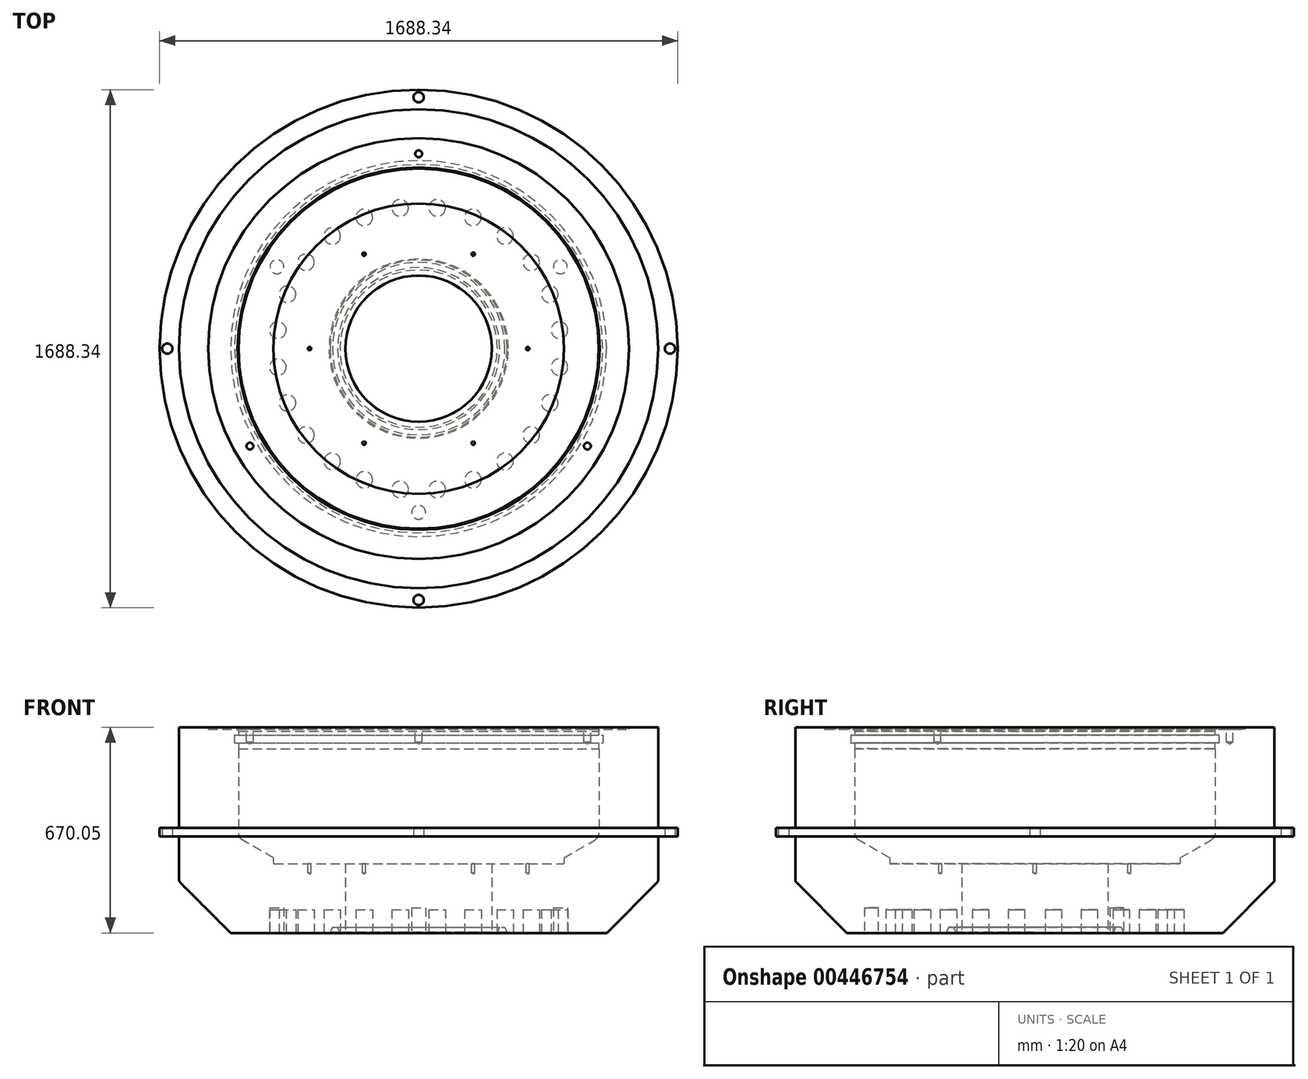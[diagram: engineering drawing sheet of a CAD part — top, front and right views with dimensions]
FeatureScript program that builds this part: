
annotation { "Feature Type Name" : "Feature", "Feature Type Description" : "" }
export const myFeature = defineFeature(function(context is Context, id is Id, definition is map)
    precondition{}
    {
        {
            var Q0;
            Q0=qCreatedBy(makeId("Right.planeOp"),FACE);
            var sketch = newSketch(context, id + "F0", { "sketchPlane" : qUnion([Q0])});
            skLineSegment(sketch, "E0", {"start": v(685.8, 0) * mm, "end": v(780.67, 0) * mm});
            skLineSegment(sketch, "E1", {"start": v(780.67, 0) * mm, "end": v(780.67, -327.03) * mm});
            skLineSegment(sketch, "E2", {"start": v(780.67, -327.03) * mm, "end": v(844.17, -327.03) * mm});
            skLineSegment(sketch, "E3", {"start": v(844.17, -327.03) * mm, "end": v(844.17, -355.6) * mm});
            skLineSegment(sketch, "E4", {"start": v(844.17, -355.6) * mm, "end": v(780.67, -355.6) * mm});
            skLineSegment(sketch, "E5", {"start": v(780.67, -355.6) * mm, "end": v(780.67, -502.16) * mm});
            skLineSegment(sketch, "E6", {"start": v(780.67, -502.16) * mm, "end": v(612.77, -670.05) * mm});
            skLineSegment(sketch, "E7", {"start": v(612.78, -670.05) * mm, "end": v(288.98, -670.05) * mm});
            skLineSegment(sketch, "E8", {"start": v(0, -670.05) * mm, "end": v(0, 0) * mm, "construction": true});
            skLineSegment(sketch, "E9", {"start": v(288.98, -670.05) * mm, "end": v(281.1, -651.5) * mm});
            skLineSegment(sketch, "E10", {"start": v(281.1, -651.5) * mm, "end": v(264.03, -651.5) * mm});
            skLineSegment(sketch, "E11", {"start": v(264.03, -651.5) * mm, "end": v(256.16, -670.05) * mm});
            skLineSegment(sketch, "E12.trimOffspring", {"start": v(256.16, -670.05) * mm, "end": v(238.32, -670.05) * mm});
            skLineSegment(sketch, "E13", {"start": v(238.32, -670.05) * mm, "end": v(238.32, -444.5) * mm});
            skLineSegment(sketch, "E14", {"start": v(238.32, -444.5) * mm, "end": v(473.14, -444.5) * mm});
            skLineSegment(sketch, "E15", {"start": v(473.14, -444.5) * mm, "end": v(473.14, -425.45) * mm});
            skLineSegment(sketch, "E16", {"start": v(473.14, -425.45) * mm, "end": v(574.68, -366.83) * mm});
            skLineSegment(sketch, "E17", {"start": v(587.38, -344.83) * mm, "end": v(587.38, -69.9) * mm});
            skLineSegment(sketch, "E18", {"start": v(587.38, -69.9) * mm, "end": v(586.61, -69.9) * mm});
            skLineSegment(sketch, "E19", {"start": v(586.61, -69.9) * mm, "end": v(586.61, -50.85) * mm});
            skLineSegment(sketch, "E20", {"start": v(586.61, -50.85) * mm, "end": v(600.08, -50.85) * mm});
            skLineSegment(sketch, "E21", {"start": v(600.08, -50.85) * mm, "end": v(600.08, -25.45) * mm});
            skLineSegment(sketch, "E22", {"start": v(600.08, -25.45) * mm, "end": v(586.61, -25.45) * mm});
            skLineSegment(sketch, "E23", {"start": v(586.61, -25.45) * mm, "end": v(586.61, -12.75) * mm});
            skLineSegment(sketch, "E24", {"start": v(586.61, -12.75) * mm, "end": v(590.28, -6.4) * mm});
            skLineSegment(sketch, "E25", {"start": v(590.28, -6.4) * mm, "end": v(685.8, -6.4) * mm});
            skLineSegment(sketch, "E26", {"start": v(685.8, -6.4) * mm, "end": v(685.8, 0) * mm});
            skPoint(sketch, "E27.visualSharp", {"position": v(587.38, -359.5) * mm});
            skArc(sketch, "E27.filletArc", {"start": v(574.68, -366.83) * mm, "mid": v(583.97, -357.53) * mm, "end": v(587.38, -344.83) * mm});
            skSolve(sketch);
        }
        {
            var Q0;
            Q0=makeQuery(id+"F0.imprint","IMPRINT",FACE,{"disambiguationData":[TD([[makeQuery(id+"F0.imprint","IMPRINT",EDGE,{"derivedFrom":sQuery(id+"F0.wireOp",EDGE,"E0")}),-1.0]])]});
            var Q1;
            Q1=sQuery(id+"F0.wireOp",EDGE,"E8");
            revolve(context, id + "F1", {"entities" : qUnion([Q0]), "axis" : qUnion([Q1]), "revolveType" : RevolveType.FULL});
        }
        {
            var Q0;
            Q0=makeQuery(id+"F1.opRevolve","SWEPT_FACE",FACE,{"disambiguationData":[OSD([sQuery(id+"F0.wireOp",EDGE,"E7")])]});
            var sketch = newSketch(context, id + "F2", { "sketchPlane" : qUnion([Q0])});
            skCircle(sketch, "E28", {"center": v(0, 0) * mm, "radius": 238.32 * mm});
            skSolve(sketch);
        }
        {
            var Q0;
            Q0=makeQuery(id+"F2.imprint","IMPRINT",FACE,{"disambiguationData":[TD([[makeQuery(id+"F2.imprint","IMPRINT",EDGE,{"derivedFrom":sQuery(id+"F2.wireOp",EDGE,"E28")}),1.0]])]});
            extrude(context, id + "F3", {"entities" : qUnion([Q0]), "operationType" : NewBodyOperationType.REMOVE, "endBound" : BoundingType.THROUGH_ALL, "oppositeDirection" : true, "depth" : 25.4 * mm});
        }
        {
            var Q0;
            Q0=makeQuery(id+"F2.imprint","IMPRINT",FACE,{"disambiguationData":[TD([[makeQuery(id+"F2.imprint","IMPRINT",EDGE,{"derivedFrom":sQuery(id+"F2.wireOp",EDGE,"E28")}),-1.0]])]});
            var sketch = newSketch(context, id + "F4", { "sketchPlane" : qUnion([Q0])});
            skCircle(sketch, "E29", {"center": v(0, 0) * mm, "radius": 533.4 * mm, "construction": true});
            skLineSegment(sketch, "E30", {"start": v(0, 576.2) * mm, "end": v(0, -586.92) * mm, "construction": true});
            skLineSegment(sketch, "E31", {"start": v(-569.53, 0) * mm, "end": v(569.53, 0) * mm, "construction": true});
            skCircle(sketch, "E32", {"center": v(0, 533.4) * mm, "radius": 22.62 * mm});
            skCircle(sketch, "E33.1.0", {"center": v(-461.94, -266.7) * mm, "radius": 22.62 * mm});
            skCircle(sketch, "E33.2.0", {"center": v(461.94, -266.7) * mm, "radius": 22.62 * mm});
            skPoint(sketch, "E34", {"position": v(-533.4, 0) * mm});
            skCircle(sketch, "E35", {"center": v(0, 0) * mm, "radius": 462.76 * mm, "construction": true});
            skCircle(sketch, "E36", {"center": v(0, 462.76) * mm, "radius": 27.01 * mm});
            skCircle(sketch, "E37.1.0", {"center": v(-119.77, 447) * mm, "radius": 27.01 * mm});
            skCircle(sketch, "E37.2.0", {"center": v(-231.38, 400.76) * mm, "radius": 27.01 * mm});
            skCircle(sketch, "E37.3.0", {"center": v(-327.22, 327.22) * mm, "radius": 27.01 * mm});
            skCircle(sketch, "E37.4.0", {"center": v(-400.76, 231.38) * mm, "radius": 27.01 * mm});
            skCircle(sketch, "E37.5.0", {"center": v(-447, 119.77) * mm, "radius": 27.01 * mm});
            skCircle(sketch, "E37.6.0", {"center": v(-462.76, 0) * mm, "radius": 27.01 * mm});
            skCircle(sketch, "E37.7.0", {"center": v(-447, -119.77) * mm, "radius": 27.01 * mm});
            skCircle(sketch, "E37.8.0", {"center": v(-400.76, -231.38) * mm, "radius": 27.01 * mm});
            skCircle(sketch, "E37.9.0", {"center": v(-327.22, -327.22) * mm, "radius": 27.01 * mm});
            skCircle(sketch, "E37.10.0", {"center": v(-231.38, -400.76) * mm, "radius": 27.01 * mm});
            skCircle(sketch, "E37.11.0", {"center": v(-119.77, -447) * mm, "radius": 27.01 * mm});
            skCircle(sketch, "E37.12.0", {"center": v(0, -462.76) * mm, "radius": 27.01 * mm});
            skCircle(sketch, "E37.13.0", {"center": v(119.77, -447) * mm, "radius": 27.01 * mm});
            skCircle(sketch, "E37.14.0", {"center": v(231.38, -400.76) * mm, "radius": 27.01 * mm});
            skCircle(sketch, "E37.15.0", {"center": v(327.22, -327.22) * mm, "radius": 27.01 * mm});
            skCircle(sketch, "E37.16.0", {"center": v(400.76, -231.38) * mm, "radius": 27.01 * mm});
            skCircle(sketch, "E37.17.0", {"center": v(447, -119.77) * mm, "radius": 27.01 * mm});
            skCircle(sketch, "E37.18.0", {"center": v(462.76, 0) * mm, "radius": 27.01 * mm});
            skCircle(sketch, "E37.19.0", {"center": v(447, 119.77) * mm, "radius": 27.01 * mm});
            skCircle(sketch, "E37.20.0", {"center": v(400.76, 231.38) * mm, "radius": 27.01 * mm});
            skCircle(sketch, "E37.21.0", {"center": v(327.22, 327.22) * mm, "radius": 27.01 * mm});
            skCircle(sketch, "E37.22.0", {"center": v(231.38, 400.76) * mm, "radius": 27.01 * mm});
            skCircle(sketch, "E37.23.0", {"center": v(119.77, 447) * mm, "radius": 27.01 * mm});
            skSolve(sketch);
        }
        {
            var Q0;
            Q0=makeQuery(id+"F4.imprint","IMPRINT",FACE,{"disambiguationData":[TD([[makeQuery(id+"F4.imprint","IMPRINT",EDGE,{"derivedFrom":sQuery(id+"F4.wireOp",EDGE,"E33.2.0")}),1.0]])]});
            var Q1;
            Q1=makeQuery(id+"F4.imprint","IMPRINT",FACE,{"disambiguationData":[TD([[makeQuery(id+"F4.imprint","IMPRINT",EDGE,{"derivedFrom":sQuery(id+"F4.wireOp",EDGE,"E32")}),1.0]])]});
            var Q2;
            Q2=makeQuery(id+"F4.imprint","IMPRINT",FACE,{"disambiguationData":[TD([[makeQuery(id+"F4.imprint","IMPRINT",EDGE,{"derivedFrom":sQuery(id+"F4.wireOp",EDGE,"E33.1.0")}),1.0]])]});
            var Q3;
            Q3=sQuery(id+"F4.wireOp",EDGE,"E32");
            var Q4;
            Q4=sQuery(id+"F4.wireOp",EDGE,"E33.2.0");
            var Q5;
            Q5=sQuery(id+"F4.wireOp",EDGE,"E33.1.0");
            extrude(context, id + "F5", {"entities" : qUnion([Q0, Q1, Q2]), "operationType" : NewBodyOperationType.REMOVE, "surfaceEntities" : qUnion([Q3, Q4, Q5]), "oppositeDirection" : true, "depth" : 82.55 * mm});
        }
        {
            var Q0;
            Q0=makeQuery(id+"F2.imprint","IMPRINT",FACE,{"disambiguationData":[TD([[makeQuery(id+"F2.imprint","IMPRINT",EDGE,{"derivedFrom":sQuery(id+"F2.wireOp",EDGE,"E28")}),-1.0]])]});
            var sketch = newSketch(context, id + "F6", { "sketchPlane" : qUnion([Q0])});
            skCircle(sketch, "E38", {"center": v(0, 0) * mm, "radius": 462.76 * mm, "construction": true});
            skLineSegment(sketch, "E39", {"start": v(0, -533.44) * mm, "end": v(0, 495.99) * mm, "construction": true});
            skLineSegment(sketch, "E40", {"start": v(-532.1, 0) * mm, "end": v(529.42, 0) * mm, "construction": true});
            skLineSegment(sketch, "E41", {"start": v(0, 0) * mm, "end": v(68.74, 522.11) * mm, "construction": true});
            skCircle(sketch, "E42", {"center": v(60.4, 458.8) * mm, "radius": 27.01 * mm});
            skCircle(sketch, "E43.1.0", {"center": v(-60.4, 458.8) * mm, "radius": 27.01 * mm});
            skCircle(sketch, "E43.2.0", {"center": v(-177.1, 427.54) * mm, "radius": 27.01 * mm});
            skCircle(sketch, "E43.3.0", {"center": v(-281.71, 367.13) * mm, "radius": 27.01 * mm});
            skCircle(sketch, "E43.4.0", {"center": v(-367.13, 281.71) * mm, "radius": 27.01 * mm});
            skCircle(sketch, "E43.5.0", {"center": v(-427.54, 177.1) * mm, "radius": 27.01 * mm});
            skCircle(sketch, "E43.6.0", {"center": v(-458.8, 60.4) * mm, "radius": 27.01 * mm});
            skCircle(sketch, "E43.7.0", {"center": v(-458.8, -60.4) * mm, "radius": 27.01 * mm});
            skCircle(sketch, "E43.8.0", {"center": v(-427.54, -177.1) * mm, "radius": 27.01 * mm});
            skCircle(sketch, "E43.9.0", {"center": v(-367.13, -281.71) * mm, "radius": 27.01 * mm});
            skCircle(sketch, "E43.10.0", {"center": v(-281.71, -367.13) * mm, "radius": 27.01 * mm});
            skCircle(sketch, "E43.11.0", {"center": v(-177.1, -427.54) * mm, "radius": 27.01 * mm});
            skCircle(sketch, "E43.12.0", {"center": v(-60.4, -458.8) * mm, "radius": 27.01 * mm});
            skCircle(sketch, "E43.13.0", {"center": v(60.4, -458.8) * mm, "radius": 27.01 * mm});
            skCircle(sketch, "E43.14.0", {"center": v(177.1, -427.54) * mm, "radius": 27.01 * mm});
            skCircle(sketch, "E43.15.0", {"center": v(281.71, -367.13) * mm, "radius": 27.01 * mm});
            skCircle(sketch, "E43.16.0", {"center": v(367.13, -281.71) * mm, "radius": 27.01 * mm});
            skCircle(sketch, "E43.17.0", {"center": v(427.54, -177.1) * mm, "radius": 27.01 * mm});
            skCircle(sketch, "E43.18.0", {"center": v(458.8, -60.4) * mm, "radius": 27.01 * mm});
            skCircle(sketch, "E43.19.0", {"center": v(458.8, 60.4) * mm, "radius": 27.01 * mm});
            skCircle(sketch, "E43.20.0", {"center": v(427.54, 177.1) * mm, "radius": 27.01 * mm});
            skCircle(sketch, "E43.21.0", {"center": v(367.13, 281.71) * mm, "radius": 27.01 * mm});
            skCircle(sketch, "E43.22.0", {"center": v(281.71, 367.13) * mm, "radius": 27.01 * mm});
            skCircle(sketch, "E43.23.0", {"center": v(177.1, 427.54) * mm, "radius": 27.01 * mm});
            skSolve(sketch);
        }
        {
            var Q0;
            Q0 = qSketchRegion(id + "F6", true);
            extrude(context, id + "F7", {"entities" : qUnion([Q0]), "operationType" : NewBodyOperationType.REMOVE, "oppositeDirection" : true, "depth" : 76.2 * mm});
        }
        {
            var Q0;
            Q0=makeQuery(id+"F1.opRevolve","SWEPT_FACE",FACE,{"disambiguationData":[OSD([sQuery(id+"F0.wireOp",EDGE,"E4")])]});
            var sketch = newSketch(context, id + "F8", { "sketchPlane" : qUnion([Q0])});
            skCircle(sketch, "E44", {"center": v(0, 0) * mm, "radius": 819.15 * mm, "construction": true});
            skLineSegment(sketch, "E45", {"start": v(0, 875.67) * mm, "end": v(0, -893.47) * mm, "construction": true});
            skLineSegment(sketch, "E46", {"start": v(-680.1, 0) * mm, "end": v(709.45, 0) * mm, "construction": true});
            skCircle(sketch, "E47", {"center": v(0, 819.15) * mm, "radius": 16.66 * mm});
            skCircle(sketch, "E48.1.0", {"center": v(-819.15, 0) * mm, "radius": 16.66 * mm});
            skCircle(sketch, "E48.2.0", {"center": v(0, -819.15) * mm, "radius": 16.66 * mm});
            skCircle(sketch, "E48.3.0", {"center": v(819.15, 0) * mm, "radius": 16.66 * mm});
            skSolve(sketch);
        }
        {
            var Q0;
            Q0 = qSketchRegion(id + "F8", true);
            extrude(context, id + "F9", {"entities" : qUnion([Q0]), "operationType" : NewBodyOperationType.REMOVE, "endBound" : BoundingType.THROUGH_ALL, "oppositeDirection" : true, "depth" : 25.4 * mm});
        }
        {
            var Q0;
            Q0=makeQuery(id+"F1.opRevolve","SWEPT_FACE",FACE,{"disambiguationData":[OSD([sQuery(id+"F0.wireOp",EDGE,"E25")])]});
            var sketch = newSketch(context, id + "F10", { "sketchPlane" : qUnion([Q0])});
            skLineSegment(sketch, "E49", {"start": v(0, 869.08) * mm, "end": v(0, -865.75) * mm, "construction": true});
            skLineSegment(sketch, "E50", {"start": v(-898.52, 0) * mm, "end": v(879.6, 0) * mm, "construction": true});
            skCircle(sketch, "E51", {"center": v(0, 0) * mm, "radius": 635 * mm, "construction": true});
            skPoint(sketch, "E52", {"position": v(0, 635) * mm});
            skPoint(sketch, "E53.1.0", {"position": v(-549.93, -317.5) * mm});
            skPoint(sketch, "E53.2.0", {"position": v(549.93, -317.5) * mm});
            skSolve(sketch);
        }
        {
            var Q0;
            Q0=sQuery(id+"F10.wireOp",VERTEX,"E52");
            var Q1;
            Q1=sQuery(id+"F10.wireOp",VERTEX,"E53.1.0");
            var Q2;
            Q2=sQuery(id+"F10.wireOp",VERTEX,"E53.2.0");
            var Q3;
            Q3=makeQuery(id+"F1.opRevolve","SWEPT_BODY",BODY,{"disambiguationData":[OSD([sQuery(id+"F0.wireOp",EDGE,"E0"),sQuery(id+"F0.wireOp",EDGE,"E1"),sQuery(id+"F0.wireOp",EDGE,"E2"),sQuery(id+"F0.wireOp",EDGE,"E3"),sQuery(id+"F0.wireOp",EDGE,"E4"),sQuery(id+"F0.wireOp",EDGE,"E5"),sQuery(id+"F0.wireOp",EDGE,"E6"),sQuery(id+"F0.wireOp",EDGE,"E7"),sQuery(id+"F0.wireOp",EDGE,"E9"),sQuery(id+"F0.wireOp",EDGE,"E10"),sQuery(id+"F0.wireOp",EDGE,"E11"),sQuery(id+"F0.wireOp",EDGE,"E12.trimOffspring"),sQuery(id+"F0.wireOp",EDGE,"E13"),sQuery(id+"F0.wireOp",EDGE,"E14"),sQuery(id+"F0.wireOp",EDGE,"E15"),sQuery(id+"F0.wireOp",EDGE,"E16"),sQuery(id+"F0.wireOp",EDGE,"E17"),sQuery(id+"F0.wireOp",EDGE,"E18"),sQuery(id+"F0.wireOp",EDGE,"E19"),sQuery(id+"F0.wireOp",EDGE,"E20"),sQuery(id+"F0.wireOp",EDGE,"E21"),sQuery(id+"F0.wireOp",EDGE,"E22"),sQuery(id+"F0.wireOp",EDGE,"E23"),sQuery(id+"F0.wireOp",EDGE,"E24"),sQuery(id+"F0.wireOp",EDGE,"E25"),sQuery(id+"F0.wireOp",EDGE,"E26"),sQuery(id+"F0.wireOp",EDGE,"E27.filletArc")])]});
            hole(context, id + "F11", {"style" : HoleStyle.SIMPLE, "endStyle" : HoleEndStyle.BLIND, "standardTappedOrClearance" : lookupTablePath({ "standard" : "ANSI", "engagement" : "75%", "pitch" : "8 tpi", "size" : "1", "type" : "Tapped" }), "standardBlindInLast" : lookupTablePath({ "standard" : "ANSI", "engagement" : "75%", "pitch" : "8 tpi", "size" : "1", "type" : "Tapped" }), "holeDiameter" : 22.22 * mm, "showTappedDepth" : true, "holeDepth" : 41.27 * mm, "isTappedThrough" : true, "tappedDepth" : 28.57 * mm, "tapClearance" : 4, "locations" : qUnion([Q0, Q1, Q2]), "scope" : qUnion([Q3]), "majorDiameter" : 25.4 * mm});
        }
        {
            var Q0;
            Q0=makeQuery(id+"F1.opRevolve","SWEPT_FACE",FACE,{"disambiguationData":[OSD([sQuery(id+"F0.wireOp",EDGE,"E14")])]});
            var sketch = newSketch(context, id + "F12", { "sketchPlane" : qUnion([Q0])});
            skLineSegment(sketch, "E54", {"start": v(-858.3, 0) * mm, "end": v(713.12, 0) * mm, "construction": true});
            skLineSegment(sketch, "E55", {"start": v(0, 688.91) * mm, "end": v(0, -536.12) * mm, "construction": true});
            skCircle(sketch, "E56", {"center": v(0, 0) * mm, "radius": 355.6 * mm, "construction": true});
            skLineSegment(sketch, "E57", {"start": v(0, 0) * mm, "end": v(-195.38, -338.41) * mm, "construction": true});
            skPoint(sketch, "E58", {"position": v(-177.8, -307.96) * mm});
            skPoint(sketch, "E59.1.0", {"position": v(177.8, -307.96) * mm});
            skPoint(sketch, "E59.2.0", {"position": v(355.6, 0) * mm});
            skPoint(sketch, "E59.3.0", {"position": v(177.8, 307.96) * mm});
            skPoint(sketch, "E59.4.0", {"position": v(-177.8, 307.96) * mm});
            skPoint(sketch, "E59.5.0", {"position": v(-355.6, 0) * mm});
            skSolve(sketch);
        }
        {
            var Q0;
            Q0=sQuery(id+"F12.wireOp",VERTEX,"E59.4.0");
            var Q1;
            Q1=sQuery(id+"F12.wireOp",VERTEX,"E59.3.0");
            var Q2;
            Q2=sQuery(id+"F12.wireOp",VERTEX,"E59.2.0");
            var Q3;
            Q3=sQuery(id+"F12.wireOp",VERTEX,"E59.1.0");
            var Q4;
            Q4=sQuery(id+"F12.wireOp",VERTEX,"E58");
            var Q5;
            Q5=sQuery(id+"F12.wireOp",VERTEX,"E59.5.0");
            var Q6;
            Q6=makeQuery(id+"F1.opRevolve","SWEPT_BODY",BODY,{"disambiguationData":[OSD([sQuery(id+"F0.wireOp",EDGE,"E0"),sQuery(id+"F0.wireOp",EDGE,"E1"),sQuery(id+"F0.wireOp",EDGE,"E2"),sQuery(id+"F0.wireOp",EDGE,"E3"),sQuery(id+"F0.wireOp",EDGE,"E4"),sQuery(id+"F0.wireOp",EDGE,"E5"),sQuery(id+"F0.wireOp",EDGE,"E6"),sQuery(id+"F0.wireOp",EDGE,"E7"),sQuery(id+"F0.wireOp",EDGE,"E9"),sQuery(id+"F0.wireOp",EDGE,"E10"),sQuery(id+"F0.wireOp",EDGE,"E11"),sQuery(id+"F0.wireOp",EDGE,"E12.trimOffspring"),sQuery(id+"F0.wireOp",EDGE,"E13"),sQuery(id+"F0.wireOp",EDGE,"E14"),sQuery(id+"F0.wireOp",EDGE,"E15"),sQuery(id+"F0.wireOp",EDGE,"E16"),sQuery(id+"F0.wireOp",EDGE,"E17"),sQuery(id+"F0.wireOp",EDGE,"E18"),sQuery(id+"F0.wireOp",EDGE,"E19"),sQuery(id+"F0.wireOp",EDGE,"E20"),sQuery(id+"F0.wireOp",EDGE,"E21"),sQuery(id+"F0.wireOp",EDGE,"E22"),sQuery(id+"F0.wireOp",EDGE,"E23"),sQuery(id+"F0.wireOp",EDGE,"E24"),sQuery(id+"F0.wireOp",EDGE,"E25"),sQuery(id+"F0.wireOp",EDGE,"E26"),sQuery(id+"F0.wireOp",EDGE,"E27.filletArc")])]});
            hole(context, id + "F13", {"style" : HoleStyle.SIMPLE, "endStyle" : HoleEndStyle.BLIND, "standardTappedOrClearance" : lookupTablePath({ "standard" : "ANSI", "engagement" : "75%", "pitch" : "13 tpi", "size" : "1/2", "type" : "Tapped" }), "standardBlindInLast" : lookupTablePath({ "standard" : "ANSI", "engagement" : "75%", "pitch" : "13 tpi", "size" : "1/2", "type" : "Tapped" }), "holeDiameter" : 10.72 * mm, "showTappedDepth" : true, "holeDepth" : 30.18 * mm, "isTappedThrough" : true, "tappedDepth" : 22.36 * mm, "tapClearance" : 4, "locations" : qUnion([Q0, Q1, Q2, Q3, Q4, Q5]), "scope" : qUnion([Q6]), "majorDiameter" : 12.7 * mm});
        }
        {
            var Q0;
            Q0=makeQuery(id+"F1.opRevolve","SWEPT_EDGE",EDGE,{"disambiguationData":[OSD([sQuery(id+"F0.wireOp",EDGE,"E5"),sQuery(id+"F0.wireOp",EDGE,"E6")])]});
            fillet(context, id + "F14", {"entities" : qUnion([Q0]), "radius" : 12.7 * mm, "tangentPropagation" : true, "allowEdgeOverflow" : false});
        }
        {
            var Q0;
            Q0=makeQuery(id+"F1.opRevolve","SWEPT_EDGE",EDGE,{"disambiguationData":[OSD([sQuery(id+"F0.wireOp",EDGE,"E7"),sQuery(id+"F0.wireOp",EDGE,"E9")])]});
            chamfer(context, id + "F15", {"entities" : qUnion([Q0]), "chamferType" : ChamferType.OFFSET_ANGLE, "width" : 1.57 * mm, "oppositeDirection" : false, "angle" : 45 * degree, "tangentPropagation" : true});
        }
        {
            var Q0;
            Q0=makeQuery(id+"F1.opRevolve","SWEPT_EDGE",EDGE,{"disambiguationData":[OSD([sQuery(id+"F0.wireOp",EDGE,"E12.trimOffspring"),sQuery(id+"F0.wireOp",EDGE,"E13")])]});
            chamfer(context, id + "F16", {"entities" : qUnion([Q0]), "chamferType" : ChamferType.OFFSET_ANGLE, "width" : 1.57 * mm, "oppositeDirection" : false, "angle" : 45 * degree, "tangentPropagation" : true});
        }
        {
            var Q0;
            Q0=makeQuery(id+"F1.opRevolve","SWEPT_EDGE",EDGE,{"disambiguationData":[OSD([sQuery(id+"F0.wireOp",EDGE,"E14"),sQuery(id+"F0.wireOp",EDGE,"E15")])]});
            fillet(context, id + "F17", {"entities" : qUnion([Q0]), "radius" : 2.3 * mm, "tangentPropagation" : true, "allowEdgeOverflow" : false});
        }
        {
            var Q0;
            Q0=makeQuery(id+"F1.opRevolve","SWEPT_EDGE",EDGE,{"disambiguationData":[OSD([sQuery(id+"F0.wireOp",EDGE,"E15"),sQuery(id+"F0.wireOp",EDGE,"E16")])]});
            fillet(context, id + "F18", {"entities" : qUnion([Q0]), "radius" : 0.76 * mm, "tangentPropagation" : true, "allowEdgeOverflow" : false});
        }
        {
            var Q0;
            Q0=makeQuery(id+"F1.opRevolve","SWEPT_EDGE",EDGE,{"disambiguationData":[OSD([sQuery(id+"F0.wireOp",EDGE,"E4"),sQuery(id+"F0.wireOp",EDGE,"E5")])]});
            fillet(context, id + "F19", {"entities" : qUnion([Q0]), "radius" : 6.35 * mm, "tangentPropagation" : true, "allowEdgeOverflow" : false});
        }
        {
            var Q0;
            Q0=makeQuery(id+"F1.opRevolve","SWEPT_EDGE",EDGE,{"disambiguationData":[OSD([sQuery(id+"F0.wireOp",EDGE,"E1"),sQuery(id+"F0.wireOp",EDGE,"E2")])]});
            fillet(context, id + "F20", {"entities" : qUnion([Q0]), "radius" : 1.6 * mm, "tangentPropagation" : true, "allowEdgeOverflow" : false});
        }
    });
